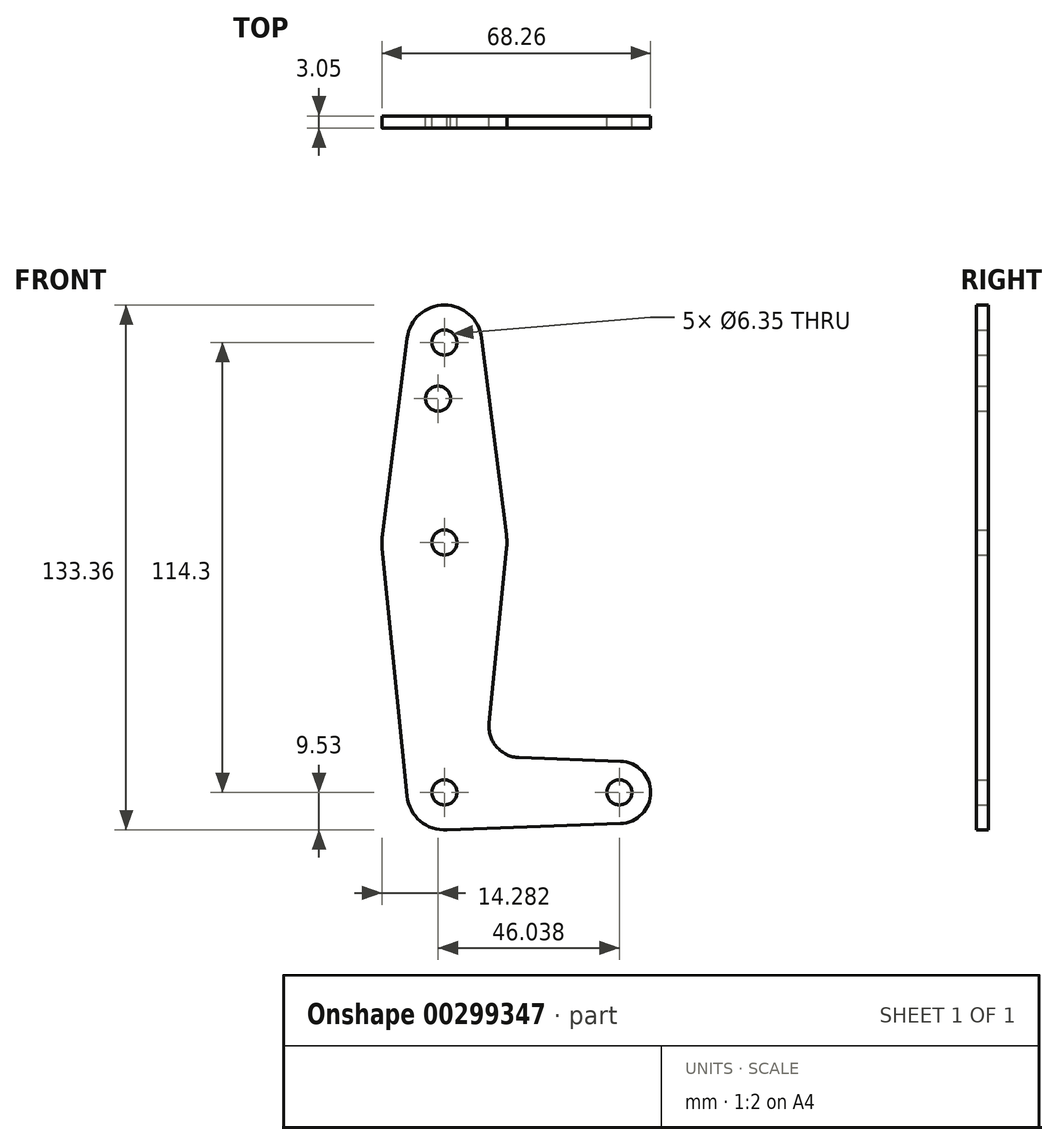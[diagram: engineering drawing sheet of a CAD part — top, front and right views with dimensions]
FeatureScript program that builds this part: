
annotation { "Feature Type Name" : "Feature", "Feature Type Description" : "" }
export const myFeature = defineFeature(function(context is Context, id is Id, definition is map)
    precondition{}
    {
        {
            var Q0;
            Q0=qCreatedBy(makeId("Front.planeOp"),FACE);
            var sketch = newSketch(context, id + "F0", { "sketchPlane" : qUnion([Q0])});
            skLineSegment(sketch, "E0", {"start": v(0, 0) * mm, "end": v(0, 114.3) * mm, "construction": true});
            skLineSegment(sketch, "E1", {"start": v(0, 0) * mm, "end": v(44.45, 0) * mm, "construction": true});
            skCircle(sketch, "E2", {"center": v(0, 114.3) * mm, "radius": 9.53 * mm});
            skCircle(sketch, "E3", {"center": v(0, 63.5) * mm, "radius": 15.88 * mm});
            skCircle(sketch, "E4", {"center": v(0, 0) * mm, "radius": 9.53 * mm});
            skCircle(sketch, "E5", {"center": v(44.45, 0) * mm, "radius": 7.94 * mm});
            skLineSegment(sketch, "E6", {"start": v(-9.45, 115.5) * mm, "end": v(-15.75, 65.48) * mm});
            skLineSegment(sketch, "E7", {"start": v(9.45, 115.5) * mm, "end": v(15.75, 65.48) * mm});
            skLineSegment(sketch, "E8", {"start": v(-15.8, 61.91) * mm, "end": v(-9.48, -0.95) * mm});
            skLineSegment(sketch, "E9", {"start": v(15.8, 61.91) * mm, "end": v(11.34, 17.59) * mm});
            skLineSegment(sketch, "E10", {"start": v(18.97, 8.85) * mm, "end": v(44.73, 7.93) * mm});
            skLineSegment(sketch, "E11", {"start": v(0, -9.52) * mm, "end": v(44.73, -7.93) * mm});
            skCircle(sketch, "E12", {"center": v(0, 63.5) * mm, "radius": 3.18 * mm});
            skCircle(sketch, "E13", {"center": v(0, 0) * mm, "radius": 3.18 * mm});
            skCircle(sketch, "E14", {"center": v(44.45, 0) * mm, "radius": 3.18 * mm});
            skCircle(sketch, "E15", {"center": v(0, 114.3) * mm, "radius": 3.18 * mm});
            skCircle(sketch, "E16", {"center": v(-1.59, 100.03) * mm, "radius": 3.18 * mm});
            skArc(sketch, "E17.filletArc", {"start": v(11.34, 17.59) * mm, "mid": v(13.26, 11.57) * mm, "end": v(18.97, 8.85) * mm});
            skSolve(sketch);
        }
        {
            var Q0;
            Q0 = qSketchRegion(id + "F0", true);
            extrude(context, id + "F1", {"entities" : qUnion([Q0]), "depth" : 3.05 * mm});
        }
    });
